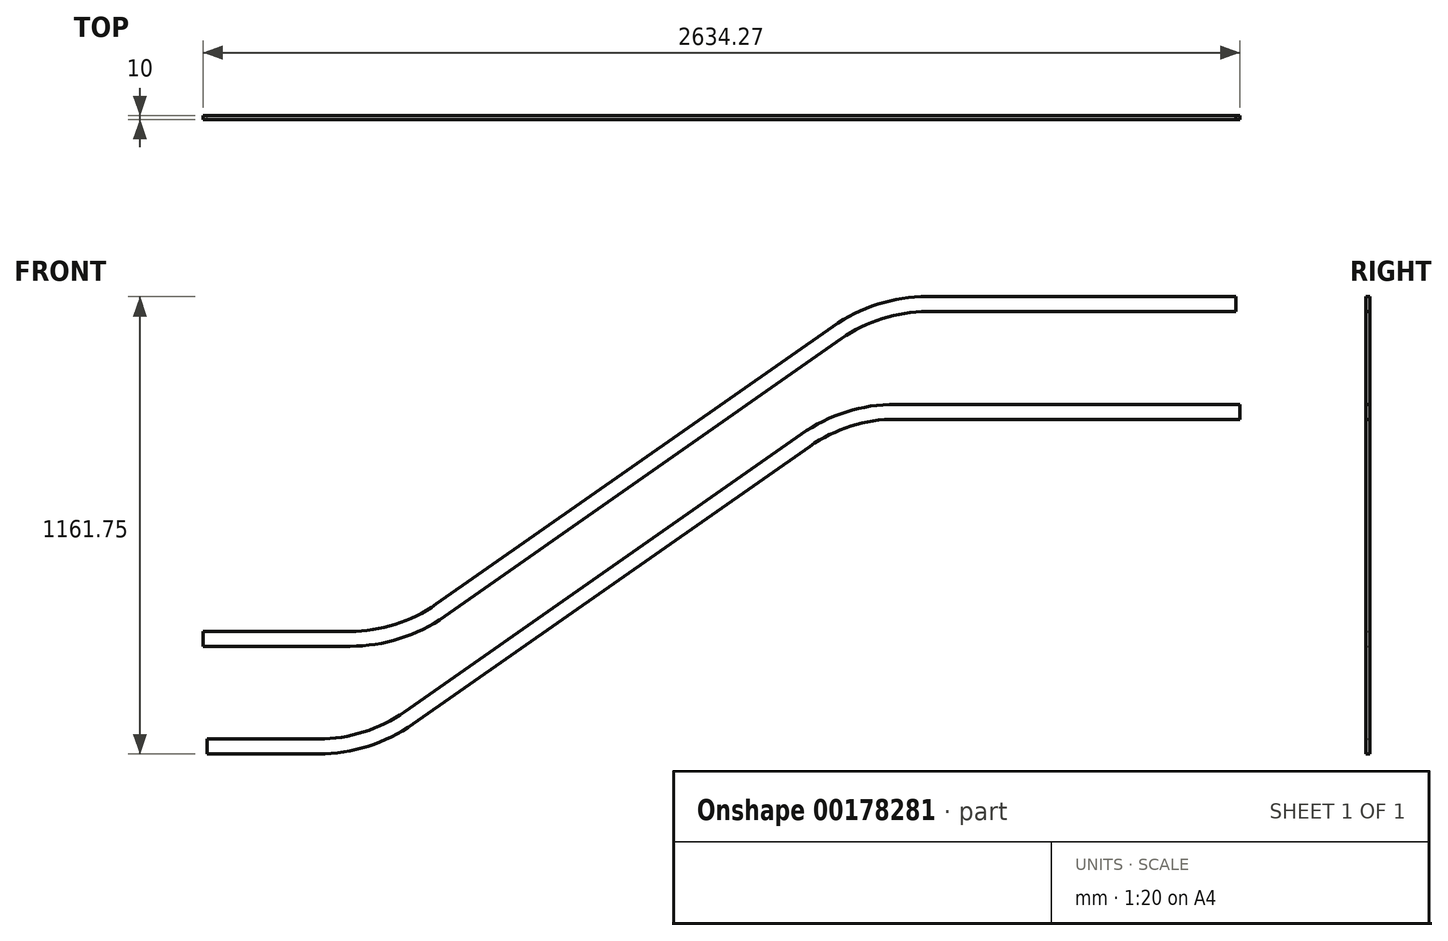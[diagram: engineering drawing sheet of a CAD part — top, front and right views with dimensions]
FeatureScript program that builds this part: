
annotation { "Feature Type Name" : "Feature", "Feature Type Description" : "" }
export const myFeature = defineFeature(function(context is Context, id is Id, definition is map)
    precondition{}
    {
        {
            var Q0;
            Q0=qCreatedBy(makeId("Front.planeOp"),FACE);
            var sketch = newSketch(context, id + "F0", { "sketchPlane" : qUnion([Q0])});
            skArc(sketch, "E0.0", {"start": v(1191.37, 1269.69) * mm, "mid": v(1191.37, 1269.69) * mm, "end": v(1191.36, 1269.69) * mm});
            skLineSegment(sketch, "E1", {"start": v(1191.36, 1269.69) * mm, "end": v(1191.37, 1269.69) * mm});
            skLineSegment(sketch, "E2", {"start": v(-506.45, 209.13) * mm, "end": v(-132.57, 209.13) * mm, "construction": true});
            skLineSegment(sketch, "E3", {"start": v(-495.96, -64.37) * mm, "end": v(-212.57, -64.37) * mm, "construction": true});
            skPoint(sketch, "E4", {"position": v(-506.45, 228.13) * mm});
            skPoint(sketch, "E5", {"position": v(-506.45, 190.13) * mm});
            skPoint(sketch, "E6", {"position": v(-495.96, -45.37) * mm});
            skPoint(sketch, "E7", {"position": v(-495.96, -83.37) * mm});
            skPoint(sketch, "E8", {"position": v(2127.82, 766.88) * mm});
            skPoint(sketch, "E9", {"position": v(2127.82, 804.88) * mm});
            skPoint(sketch, "E10", {"position": v(2117.82, 1040.38) * mm});
            skPoint(sketch, "E11", {"position": v(2117.82, 1078.38) * mm});
            skPoint(sketch, "E12.visualSharp", {"position": v(-6.45, 209.13) * mm});
            skPoint(sketch, "E13.visualSharp", {"position": v(-86.45, -64.37) * mm});
            skPoint(sketch, "E14.visualSharp", {"position": v(1127.82, 785.88) * mm});
            skPoint(sketch, "E15.visualSharp", {"position": v(1207.82, 1059.38) * mm});
            skLineSegment(sketch, "E16", {"start": v(2127.82, 766.88) * mm, "end": v(2127.82, 804.88) * mm});
            skLineSegment(sketch, "E17", {"start": v(2117.82, 1040.38) * mm, "end": v(2117.82, 1078.38) * mm});
            skPoint(sketch, "E18.end.orphan", {"position": v(2127.82, 785.88) * mm});
            skPoint(sketch, "E19.end.orphan", {"position": v(2117.82, 1059.38) * mm});
            skLineSegment(sketch, "E20", {"start": v(1253.94, 785.88) * mm, "end": v(2127.82, 785.88) * mm, "construction": true});
            skLineSegment(sketch, "E21", {"start": v(1333.94, 1059.38) * mm, "end": v(2117.82, 1059.38) * mm, "construction": true});
            skLineSegment(sketch, "E22", {"start": v(96.86, 281.47) * mm, "end": v(1104.51, 987.04) * mm, "construction": true});
            skLineSegment(sketch, "E23", {"start": v(16.86, 7.97) * mm, "end": v(1024.51, 713.54) * mm, "construction": true});
            skArc(sketch, "E24.filletArc", {"start": v(-212.57, -64.37) * mm, "mid": v(-92.3, -45.86) * mm, "end": v(16.86, 7.97) * mm, "construction": true});
            skArc(sketch, "E25.filletArc", {"start": v(-132.57, 209.13) * mm, "mid": v(-12.3, 227.64) * mm, "end": v(96.86, 281.47) * mm, "construction": true});
            skArc(sketch, "E26.filletArc", {"start": v(1253.94, 785.88) * mm, "mid": v(1133.66, 767.36) * mm, "end": v(1024.51, 713.54) * mm, "construction": true});
            skArc(sketch, "E27.filletArc", {"start": v(1333.94, 1059.38) * mm, "mid": v(1213.66, 1040.86) * mm, "end": v(1104.51, 987.04) * mm, "construction": true});
            skLineSegment(sketch, "E28", {"start": v(-506.45, 190.13) * mm, "end": v(-506.45, 228.13) * mm});
            skLineSegment(sketch, "E29", {"start": v(-495.96, -83.37) * mm, "end": v(-495.96, -45.37) * mm});
            skArc(sketch, "E30.0", {"start": v(-212.57, -83.37) * mm, "mid": v(-86.58, -63.98) * mm, "end": v(27.75, -7.6) * mm});
            skArc(sketch, "E31.0", {"start": v(-212.57, -45.37) * mm, "mid": v(-98, -27.74) * mm, "end": v(5.96, 23.53) * mm});
            skArc(sketch, "E32.0", {"start": v(-132.57, 190.13) * mm, "mid": v(-6.58, 209.52) * mm, "end": v(107.75, 265.9) * mm});
            skArc(sketch, "E33.0", {"start": v(-132.57, 228.13) * mm, "mid": v(-18, 245.76) * mm, "end": v(85.96, 297.03) * mm});
            skArc(sketch, "E34.0", {"start": v(1253.94, 804.88) * mm, "mid": v(1127.95, 785.48) * mm, "end": v(1013.61, 729.1) * mm});
            skArc(sketch, "E35.0", {"start": v(1253.94, 766.88) * mm, "mid": v(1139.37, 749.24) * mm, "end": v(1035.4, 697.97) * mm});
            skArc(sketch, "E36.0", {"start": v(1333.94, 1078.38) * mm, "mid": v(1207.95, 1058.98) * mm, "end": v(1093.61, 1002.6) * mm});
            skArc(sketch, "E37.0", {"start": v(1333.94, 1040.38) * mm, "mid": v(1219.37, 1022.74) * mm, "end": v(1115.4, 971.47) * mm});
            skLineSegment(sketch, "E38", {"start": v(2117.82, 1040.38) * mm, "end": v(1333.94, 1040.38) * mm});
            skLineSegment(sketch, "E39", {"start": v(1333.94, 1078.38) * mm, "end": v(2117.82, 1078.38) * mm});
            skLineSegment(sketch, "E40", {"start": v(2127.82, 804.88) * mm, "end": v(1253.94, 804.88) * mm});
            skLineSegment(sketch, "E41", {"start": v(1253.94, 766.88) * mm, "end": v(2127.82, 766.88) * mm});
            skLineSegment(sketch, "E42", {"start": v(27.75, -7.6) * mm, "end": v(1035.4, 697.97) * mm});
            skLineSegment(sketch, "E43", {"start": v(1013.61, 729.1) * mm, "end": v(5.96, 23.53) * mm});
            skLineSegment(sketch, "E44", {"start": v(107.75, 265.9) * mm, "end": v(1115.4, 971.47) * mm});
            skLineSegment(sketch, "E45", {"start": v(1093.61, 1002.6) * mm, "end": v(85.96, 297.03) * mm});
            skLineSegment(sketch, "E46", {"start": v(-132.57, 190.13) * mm, "end": v(-506.45, 190.13) * mm});
            skLineSegment(sketch, "E47", {"start": v(-506.45, 228.13) * mm, "end": v(-132.57, 228.13) * mm});
            skLineSegment(sketch, "E48", {"start": v(-212.57, -45.37) * mm, "end": v(-495.96, -45.37) * mm});
            skLineSegment(sketch, "E49", {"start": v(-495.96, -83.37) * mm, "end": v(-212.57, -83.37) * mm});
            skSolve(sketch);
        }
        {
            var Q0;
            Q0=qSketchRegion(id+"F0",true);
            extrude(context, id + "F1", {"entities" : qUnion([Q0]), "depth" : 10 * mm});
        }
    });
